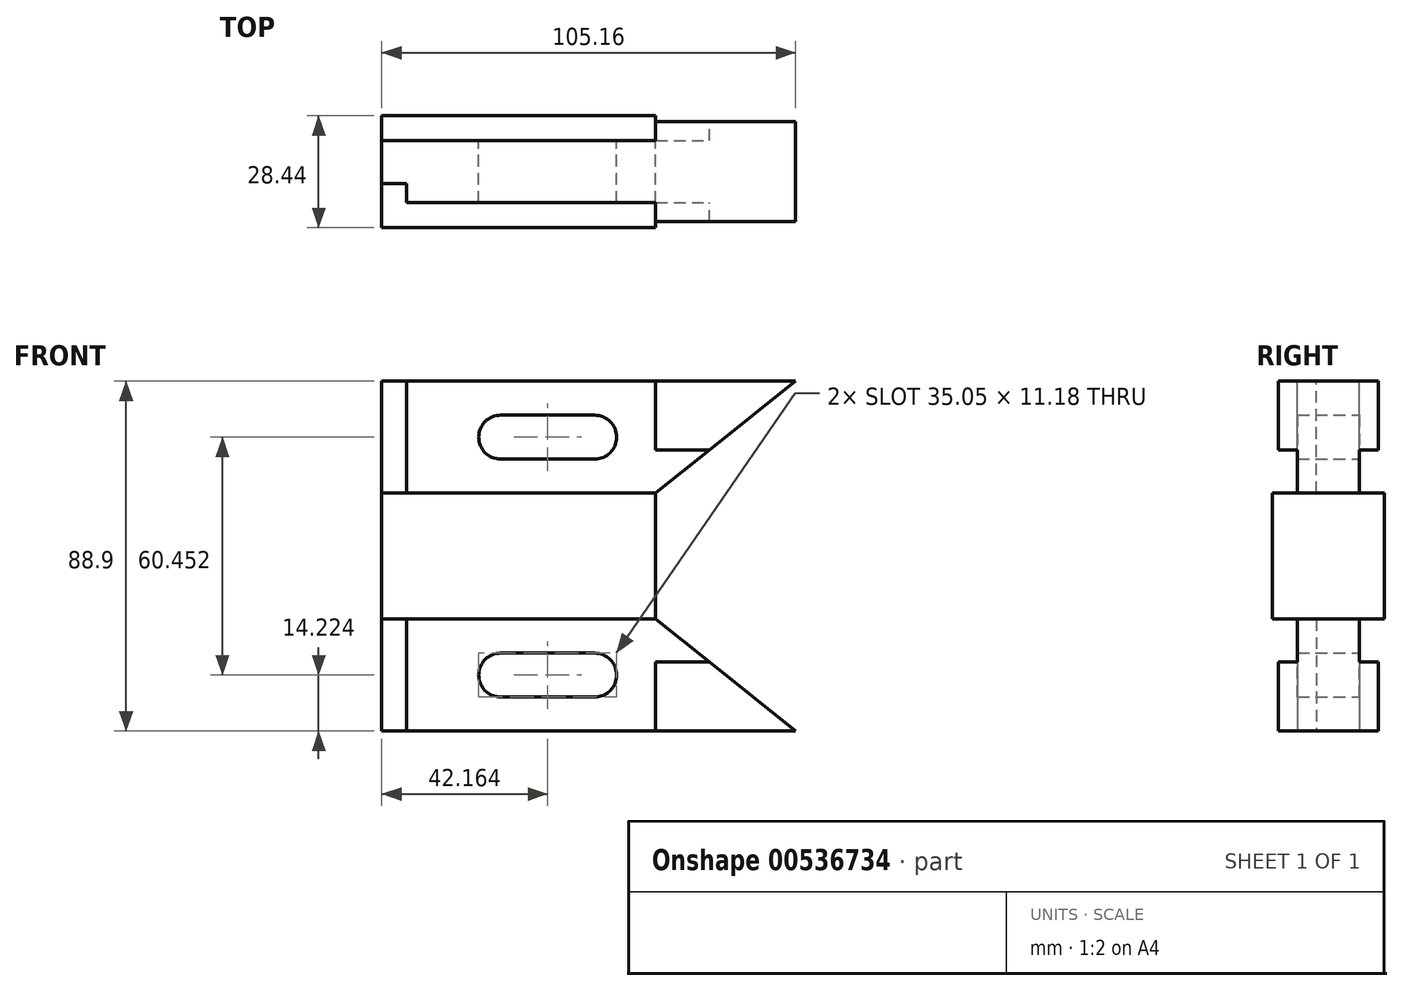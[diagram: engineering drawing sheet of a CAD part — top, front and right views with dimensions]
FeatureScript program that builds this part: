
annotation { "Feature Type Name" : "Feature", "Feature Type Description" : "" }
export const myFeature = defineFeature(function(context is Context, id is Id, definition is map)
    precondition{}
    {
        {
            var Q0;
            Q0=qCreatedBy(makeId("Front.planeOp"),FACE);
            var sketch = newSketch(context, id + "F0", { "sketchPlane" : qUnion([Q0])});
            skLineSegment(sketch, "E0", {"start": v(0, 0) * mm, "end": v(0, 16) * mm});
            skLineSegment(sketch, "E1", {"start": v(0, 16) * mm, "end": v(69.6, 16) * mm});
            skLineSegment(sketch, "E2", {"start": v(69.6, 0) * mm, "end": v(69.6, 16) * mm});
            skLineSegment(sketch, "E3", {"start": v(0, 16) * mm, "end": v(0, 44.45) * mm});
            skLineSegment(sketch, "E4", {"start": v(0, 44.45) * mm, "end": v(105.16, 44.45) * mm});
            skLineSegment(sketch, "E5", {"start": v(69.6, 16) * mm, "end": v(105.16, 44.45) * mm});
            skLineSegment(sketch, "E6", {"start": v(0, 16) * mm, "end": v(6.35, 16) * mm, "construction": true});
            skLineSegment(sketch, "E7", {"start": v(6.35, 16) * mm, "end": v(6.35, 44.45) * mm});
            skLineSegment(sketch, "E8", {"start": v(0, 16) * mm, "end": v(24.64, 16) * mm, "construction": true});
            skLineSegment(sketch, "E9", {"start": v(24.64, 30.23) * mm, "end": v(24.64, 30.23) * mm});
            skLineSegment(sketch, "E10", {"start": v(30.23, 35.81) * mm, "end": v(54.1, 35.81) * mm});
            skLineSegment(sketch, "E11", {"start": v(59.69, 30.23) * mm, "end": v(59.69, 30.23) * mm});
            skLineSegment(sketch, "E12", {"start": v(59.69, 30.23) * mm, "end": v(24.64, 30.23) * mm, "construction": true});
            skLineSegment(sketch, "E13.MirrorCS", {"start": v(30.23, 24.64) * mm, "end": v(54.1, 24.64) * mm});
            skPoint(sketch, "E14.visualSharp", {"position": v(24.64, 35.81) * mm});
            skArc(sketch, "E14.filletArc", {"start": v(30.23, 35.81) * mm, "mid": v(26.27, 34.18) * mm, "end": v(24.64, 30.23) * mm});
            skPoint(sketch, "E15.visualSharp", {"position": v(24.64, 24.64) * mm});
            skArc(sketch, "E15.filletArc", {"start": v(24.64, 30.23) * mm, "mid": v(26.27, 26.27) * mm, "end": v(30.23, 24.64) * mm});
            skPoint(sketch, "E16.visualSharp", {"position": v(59.69, 35.81) * mm});
            skArc(sketch, "E16.filletArc", {"start": v(59.69, 30.23) * mm, "mid": v(58.05, 34.18) * mm, "end": v(54.1, 35.81) * mm});
            skPoint(sketch, "E17.visualSharp", {"position": v(59.69, 24.64) * mm});
            skArc(sketch, "E17.filletArc", {"start": v(54.1, 24.64) * mm, "mid": v(58.05, 26.27) * mm, "end": v(59.7, 30.23) * mm});
            skLineSegment(sketch, "E18", {"start": v(69.6, 26.92) * mm, "end": v(69.6, 44.45) * mm});
            skLineSegment(sketch, "E19", {"start": v(69.6, 26.92) * mm, "end": v(83.25, 26.92) * mm});
            skArc(sketch, "E20.MirrorCS", {"start": v(30.23, -35.81) * mm, "mid": v(26.27, -34.18) * mm, "end": v(24.64, -30.23) * mm});
            skLineSegment(sketch, "E21.MirrorCS", {"start": v(0, -16) * mm, "end": v(6.35, -16) * mm, "construction": true});
            skArc(sketch, "E22.MirrorCS", {"start": v(24.64, -30.23) * mm, "mid": v(26.27, -26.27) * mm, "end": v(30.23, -24.64) * mm});
            skArc(sketch, "E23.MirrorCS", {"start": v(54.1, -24.64) * mm, "mid": v(58.05, -26.27) * mm, "end": v(59.7, -30.23) * mm});
            skArc(sketch, "E24.MirrorCS", {"start": v(59.69, -30.23) * mm, "mid": v(58.05, -34.18) * mm, "end": v(54.1, -35.81) * mm});
            skLineSegment(sketch, "E25.MirrorCS", {"start": v(24.64, -30.23) * mm, "end": v(24.64, -30.23) * mm});
            skLineSegment(sketch, "E26.MirrorCS", {"start": v(59.69, -30.23) * mm, "end": v(59.69, -30.23) * mm});
            skLineSegment(sketch, "E27.MirrorCS", {"start": v(30.23, -24.64) * mm, "end": v(54.1, -24.64) * mm});
            skLineSegment(sketch, "E28.MirrorCS", {"start": v(59.69, -30.23) * mm, "end": v(24.64, -30.23) * mm, "construction": true});
            skLineSegment(sketch, "E29.MirrorCS", {"start": v(69.6, -26.92) * mm, "end": v(69.6, -44.45) * mm});
            skPoint(sketch, "E30.MirrorP", {"position": v(59.69, -24.64) * mm});
            skLineSegment(sketch, "E31.MirrorCS", {"start": v(30.23, -35.81) * mm, "end": v(54.1, -35.81) * mm});
            skLineSegment(sketch, "E32.MirrorCS", {"start": v(69.6, -16) * mm, "end": v(105.16, -44.45) * mm});
            skLineSegment(sketch, "E33.MirrorCS", {"start": v(0, -44.45) * mm, "end": v(105.16, -44.45) * mm});
            skLineSegment(sketch, "E34.MirrorCS", {"start": v(6.35, -16) * mm, "end": v(6.35, -44.45) * mm});
            skLineSegment(sketch, "E35.MirrorCS", {"start": v(0, -16) * mm, "end": v(0, -44.45) * mm});
            skLineSegment(sketch, "E36.MirrorCS", {"start": v(69.6, -26.92) * mm, "end": v(83.25, -26.92) * mm});
            skPoint(sketch, "E37.MirrorP", {"position": v(24.64, -35.81) * mm});
            skLineSegment(sketch, "E38.MirrorCS", {"start": v(0, -16) * mm, "end": v(24.64, -16) * mm, "construction": true});
            skLineSegment(sketch, "E39.MirrorCS", {"start": v(69.6, 0) * mm, "end": v(69.6, -16) * mm});
            skLineSegment(sketch, "E40.MirrorCS", {"start": v(0, -16) * mm, "end": v(69.6, -16) * mm});
            skLineSegment(sketch, "E41.MirrorCS", {"start": v(0, 0) * mm, "end": v(0, -16) * mm});
            skPoint(sketch, "E42.MirrorP", {"position": v(59.69, -35.81) * mm});
            skPoint(sketch, "E43.MirrorP", {"position": v(24.64, -24.64) * mm});
            skSolve(sketch);
        }
        {
            var Q0;
            {var subQ3=sQuery(id+"F0.wireOp",EDGE,"E7");Q0=makeQuery(id+"F0.imprint","IMPRINT",FACE,{"disambiguationData":[TD([[makeQuery(id+"F0.imprint","IMPRINT",EDGE,{"derivedFrom":subQ3}),-1.0]])]});}
            extrude(context, id + "F1", {"entities" : qUnion([Q0]), "endBound" : BoundingType.SYMMETRIC, "depth" : 15.75 * mm, "offsetDistance" : 25.4 * mm});
        }
        {
            var Q0;
            {var subQ7=sQuery(id+"F0.wireOp",EDGE,"E0");Q0=makeQuery(id+"F0.imprint","IMPRINT",FACE,{"disambiguationData":[TD([[makeQuery(id+"F0.imprint","IMPRINT",EDGE,{"derivedFrom":subQ7}),-1.0]])]});}
            extrude(context, id + "F2", {"entities" : qUnion([Q0]), "operationType" : NewBodyOperationType.ADD, "endBound" : BoundingType.SYMMETRIC, "depth" : 28.45 * mm, "offsetDistance" : 25.4 * mm});
        }
        {
            var Q0;
            {var subQ3=sQuery(id+"F0.wireOp",EDGE,"E18");Q0=makeQuery(id+"F0.imprint","IMPRINT",FACE,{"disambiguationData":[TD([[makeQuery(id+"F0.imprint","IMPRINT",EDGE,{"derivedFrom":subQ3}),-1.0]])]});}
            extrude(context, id + "F3", {"entities" : qUnion([Q0]), "operationType" : NewBodyOperationType.ADD, "endBound" : BoundingType.SYMMETRIC, "depth" : 25.4 * mm, "offsetDistance" : 25.4 * mm});
        }
        {
            var Q0;
            {var subQ0=sQuery(id+"F0.wireOp",EDGE,"E3");Q0=makeQuery(id+"F0.imprint","IMPRINT",FACE,{"disambiguationData":[TD([[makeQuery(id+"F0.imprint","IMPRINT",EDGE,{"derivedFrom":subQ0}),-1.0]])]});}
            extrude(context, id + "F4", {"entities" : qUnion([Q0]), "operationType" : NewBodyOperationType.ADD, "depth" : -7.87 * mm, "offsetDistance" : 25.4 * mm});
        }
        {
            var Q0;
            {var subQ0=sQuery(id+"F0.wireOp",EDGE,"E3");Q0=makeQuery(id+"F0.imprint","IMPRINT",FACE,{"disambiguationData":[TD([[makeQuery(id+"F0.imprint","IMPRINT",EDGE,{"derivedFrom":subQ0}),-1.0]])]});}
            extrude(context, id + "F5", {"entities" : qUnion([Q0]), "operationType" : NewBodyOperationType.ADD, "depth" : 3.05 * mm, "offsetDistance" : 25.4 * mm});
        }
        {
            var Q0;
            Q0=makeQuery(id+"F1.opExtrude","SWEPT_BODY",BODY,{"disambiguationData":[OSD([sQuery(id+"F0.wireOp",EDGE,"E1"),sQuery(id+"F0.wireOp",EDGE,"E4"),sQuery(id+"F0.wireOp",EDGE,"E5"),sQuery(id+"F0.wireOp",EDGE,"E7"),sQuery(id+"F0.wireOp",EDGE,"E10"),sQuery(id+"F0.wireOp",EDGE,"E13.MirrorCS"),sQuery(id+"F0.wireOp",EDGE,"E14.filletArc"),sQuery(id+"F0.wireOp",EDGE,"E15.filletArc"),sQuery(id+"F0.wireOp",EDGE,"E16.filletArc"),sQuery(id+"F0.wireOp",EDGE,"E17.filletArc"),sQuery(id+"F0.wireOp",EDGE,"E18"),sQuery(id+"F0.wireOp",EDGE,"E19")])]});
            var Q1;
            Q1=qCreatedBy(makeId("Top.planeOp"),FACE);
            mirror(context, id + "F6", {"operationType" : NewBodyOperationType.ADD, "entities" : qUnion([Q0]), "mirrorPlane" : qUnion([Q1])});
        }
    });
